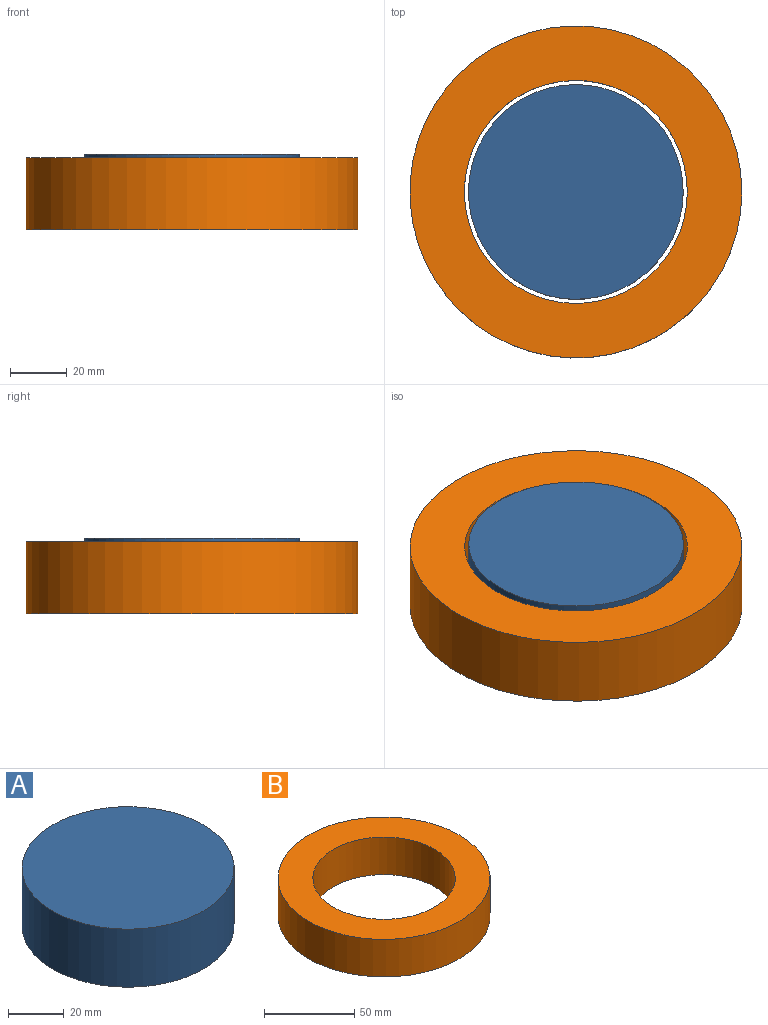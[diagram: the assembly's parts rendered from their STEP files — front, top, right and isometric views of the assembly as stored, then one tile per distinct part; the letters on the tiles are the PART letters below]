
ASSEMBLY  parts=2 mates=1
PART A: 3 faces, bbox 75.8x75.8x25.4 mm
  f0: cylinder r=37.91mm len=75.83mm, axis (0,0,-1), area 6050.8mm2, adj f1,f2
  f1: plane 75.83x75.83mm, normal (0,0,1), area 4515.9mm2, adj f0
  f2: plane 75.83x75.83mm, normal (0,0,-1), area 4515.9mm2, adj f0
PART B: 4 faces, bbox 117.3x117.3x25.4 mm
  f0: cylinder r=39.37mm len=78.74mm, axis (0,0,-1), area 6282.9mm2, adj f2,f3
  f1: cylinder r=58.64mm len=117.28mm, axis (0,0,-1), area 9358.2mm2, adj f2,f3
  f2: plane 117.28x117.28mm, normal (0,0,1), area 5933mm2, adj f0,f1
  f3: plane 117.28x117.28mm, normal (0,0,-1), area 5933mm2, adj f0,f1
PLACE A rot(axis=(0,0,-1),0.5deg) t=(0,0,1.11)mm
PLACE B at identity fixed
MATE cylindrical A.f0 <-> B.f0  axis (0,0,1) through (0,0,26.51)mm
